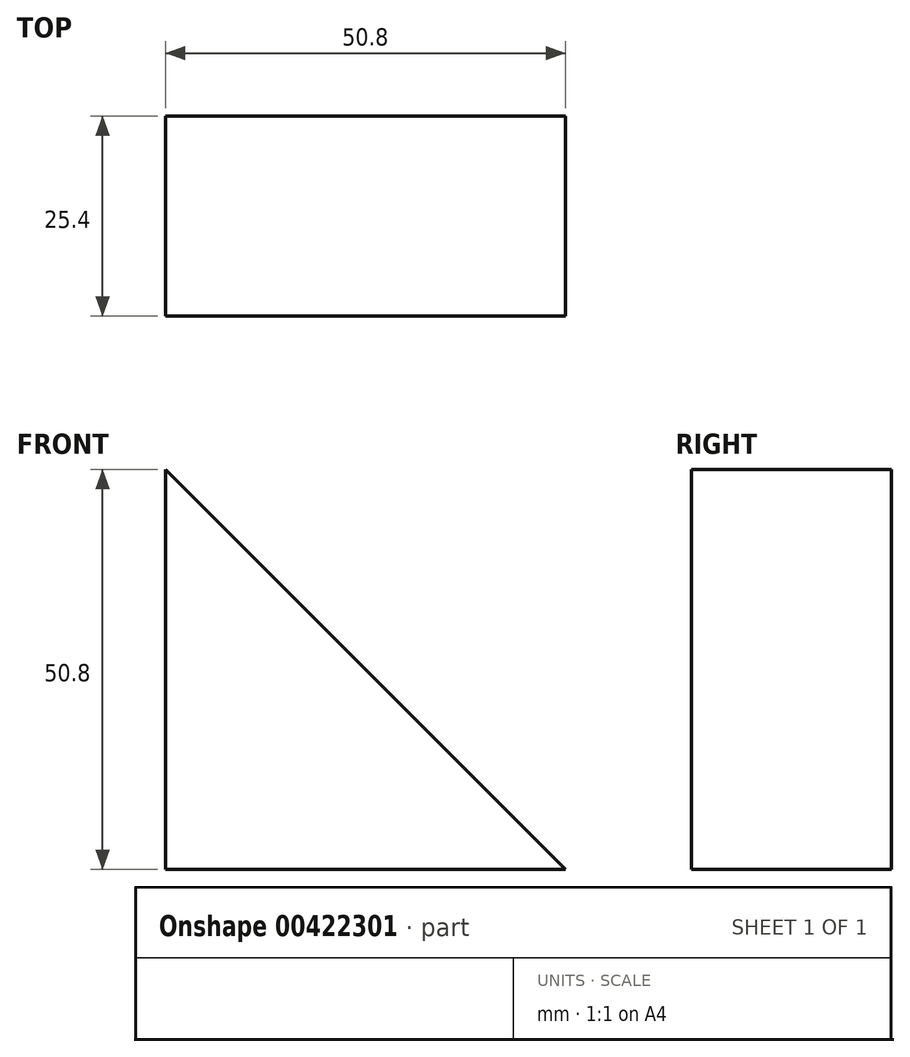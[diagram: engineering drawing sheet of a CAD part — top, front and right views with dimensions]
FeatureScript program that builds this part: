
annotation { "Feature Type Name" : "Feature", "Feature Type Description" : "" }
export const myFeature = defineFeature(function(context is Context, id is Id, definition is map)
    precondition{}
    {
        {
            var Q0;
            Q0=qCreatedBy(makeId("Front.planeOp"),FACE);
            var sketch = newSketch(context, id + "F0", { "sketchPlane" : qUnion([Q0])});
            skLineSegment(sketch, "E0", {"start": v(-40.77, -29.62) * mm, "end": v(-40.77, 21.18) * mm});
            skLineSegment(sketch, "E1", {"start": v(-40.77, -29.62) * mm, "end": v(10.03, -29.62) * mm});
            skLineSegment(sketch, "E2", {"start": v(10.03, -29.62) * mm, "end": v(-40.77, 21.18) * mm});
            skSolve(sketch);
        }
        {
            var Q0;
            Q0=makeQuery(id+"F0.imprint","IMPRINT",FACE,{"disambiguationData":[TD([[makeQuery(id+"F0.imprint","IMPRINT",EDGE,{"derivedFrom":sQuery(id+"F0.wireOp",EDGE,"E0")}),-1.0]])]});
            extrude(context, id + "F1", {"entities" : qUnion([Q0]), "depth" : 25.4 * mm});
        }
    });
